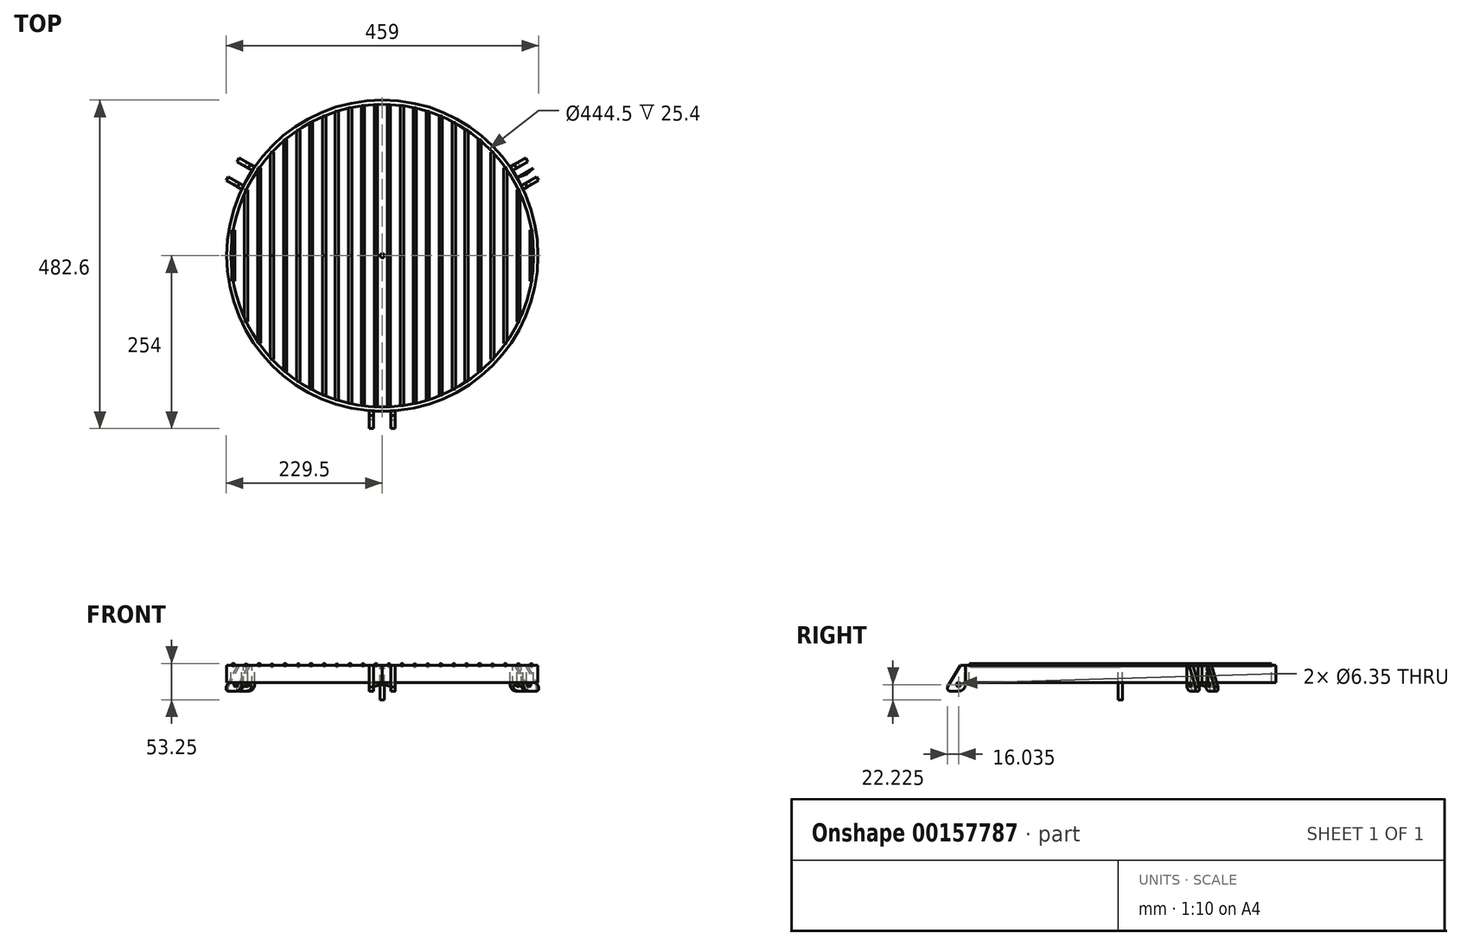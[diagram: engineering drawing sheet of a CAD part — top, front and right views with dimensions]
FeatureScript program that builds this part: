
annotation { "Feature Type Name" : "Feature", "Feature Type Description" : "" }
export const myFeature = defineFeature(function(context is Context, id is Id, definition is map)
    precondition{}
    {
        {
            var Q0;
            Q0=qCreatedBy(makeId("Top.planeOp"),FACE);
            var sketch = newSketch(context, id + "F0", { "sketchPlane" : qUnion([Q0])});
            skCircle(sketch, "E0", {"center": v(0, 0) * mm, "radius": 228.6 * mm});
            skLineSegment(sketch, "E1", {"start": v(-131.22, 187.18) * mm, "end": v(0, 0) * mm});
            skLineSegment(sketch, "E2", {"start": v(0, 0) * mm, "end": v(-96.5, -207.24) * mm});
            skLineSegment(sketch, "E3", {"start": v(0, 0) * mm, "end": v(227.72, 20.05) * mm});
            skPoint(sketch, "E4", {"position": v(-93.81, -201.48) * mm});
            skPoint(sketch, "E5", {"position": v(-127.58, 181.98) * mm});
            skPoint(sketch, "E6", {"position": v(221.4, 19.5) * mm});
            skCircle(sketch, "E7", {"center": v(0, 0) * mm, "radius": 222.25 * mm});
            skPoint(sketch, "E8", {"position": v(227.72, 20.05) * mm});
            skPoint(sketch, "E9", {"position": v(-96.5, -207.24) * mm});
            skPoint(sketch, "E10", {"position": v(-131.22, 187.18) * mm});
            skCircle(sketch, "E11", {"center": v(0, 0) * mm, "radius": 3.18 * mm});
            skSolve(sketch);
        }
        {
            var Q0;
            {var subQ0=sQuery(id+"F0.wireOp",EDGE,"E1");var subQ1=sQuery(id+"F0.wireOp",EDGE,"E0");var subQ2=makeQuery(id+"F0.imprint","INTERSECT",VERTEX,{"derivedFrom":[subQ1,subQ0]});Q0=makeQuery(id+"F0.imprint","IMPRINT",FACE,{"disambiguationData":[TD([[makeQuery(id+"F0.imprint","IMPRINT",EDGE,{"disambiguationData":[TD([[subQ2,-1.0]])],"derivedFrom":subQ1}),1.0]])]});}
            var Q1;
            {var subQ0=sQuery(id+"F0.wireOp",EDGE,"E2");var subQ1=sQuery(id+"F0.wireOp",EDGE,"E0");var subQ2=makeQuery(id+"F0.imprint","INTERSECT",VERTEX,{"derivedFrom":[subQ1,subQ0]});Q1=makeQuery(id+"F0.imprint","IMPRINT",FACE,{"disambiguationData":[TD([[makeQuery(id+"F0.imprint","IMPRINT",EDGE,{"disambiguationData":[TD([[subQ2,-1.0]])],"derivedFrom":subQ1}),1.0]])]});}
            var Q2;
            {var subQ0=sQuery(id+"F0.wireOp",EDGE,"E1");var subQ1=sQuery(id+"F0.wireOp",EDGE,"E0");var subQ2=makeQuery(id+"F0.imprint","INTERSECT",VERTEX,{"derivedFrom":[subQ1,subQ0]});Q2=makeQuery(id+"F0.imprint","IMPRINT",FACE,{"disambiguationData":[TD([[makeQuery(id+"F0.imprint","IMPRINT",EDGE,{"disambiguationData":[TD([[subQ2,1.0]])],"derivedFrom":subQ1}),1.0]])]});}
            extrude(context, id + "F1", {"entities" : qUnion([Q0, Q1, Q2]), "oppositeDirection" : true, "depth" : 25.4 * mm});
        }
        {
            var Q0;
            Q0=qCreatedBy(makeId("Top.planeOp"),FACE);
            var sketch = newSketch(context, id + "F2", { "sketchPlane" : qUnion([Q0])});
            skLineSegment(sketch, "E12", {"start": v(-221.98, 0) * mm, "end": v(222.25, 0) * mm});
            skPoint(sketch, "E13", {"position": v(-9.53, 0) * mm});
            skPoint(sketch, "E14", {"position": v(9.53, 0) * mm});
            skPoint(sketch, "E15", {"position": v(28.57, 0) * mm});
            skPoint(sketch, "E16", {"position": v(66.67, 0) * mm});
            skPoint(sketch, "E17", {"position": v(47.62, 0) * mm});
            skPoint(sketch, "E18", {"position": v(85.72, 0) * mm});
            skPoint(sketch, "E19", {"position": v(104.77, 0) * mm});
            skPoint(sketch, "E20", {"position": v(123.82, 0) * mm});
            skPoint(sketch, "E21", {"position": v(142.88, 0) * mm});
            skPoint(sketch, "E22", {"position": v(161.93, 0) * mm});
            skPoint(sketch, "E23", {"position": v(180.98, 0) * mm});
            skPoint(sketch, "E24", {"position": v(200.03, 0) * mm});
            skPoint(sketch, "E25", {"position": v(219.08, 0) * mm});
            skPoint(sketch, "E26", {"position": v(-28.57, 0) * mm});
            skPoint(sketch, "E27", {"position": v(-47.62, 0) * mm});
            skPoint(sketch, "E28", {"position": v(-66.67, 0) * mm});
            skPoint(sketch, "E29", {"position": v(-85.72, 0) * mm});
            skPoint(sketch, "E30", {"position": v(-104.77, 0) * mm});
            skPoint(sketch, "E31", {"position": v(-123.82, 0) * mm});
            skPoint(sketch, "E32", {"position": v(-142.88, 0) * mm});
            skPoint(sketch, "E33", {"position": v(-161.93, 0) * mm});
            skPoint(sketch, "E34", {"position": v(-180.98, 0) * mm});
            skPoint(sketch, "E35", {"position": v(-200.03, 0) * mm});
            skPoint(sketch, "E36", {"position": v(-219.08, 0) * mm});
            skSolve(sketch);
        }
        {
            var Q0;
            Q0=qCreatedBy(makeId("Front.planeOp"),FACE);
            var sketch = newSketch(context, id + "F3", { "sketchPlane" : qUnion([Q0])});
            skCircle(sketch, "E37", {"center": v(-219.08, 0) * mm, "radius": 2.38 * mm});
            skCircle(sketch, "E38", {"center": v(-200.35, -0.55) * mm, "radius": 2.38 * mm});
            skCircle(sketch, "E39", {"center": v(-180.87, 0.07) * mm, "radius": 2.38 * mm});
            skCircle(sketch, "E40", {"center": v(-162.2, -0.64) * mm, "radius": 2.38 * mm});
            skCircle(sketch, "E41", {"center": v(-143.01, 0.04) * mm, "radius": 2.38 * mm});
            skCircle(sketch, "E42", {"center": v(-123.47, -0.4) * mm, "radius": 2.38 * mm});
            skCircle(sketch, "E43", {"center": v(-104.72, 0) * mm, "radius": 2.38 * mm});
            skCircle(sketch, "E44", {"center": v(-85.3, -0.08) * mm, "radius": 2.38 * mm});
            skCircle(sketch, "E45", {"center": v(-66.89, -0.46) * mm, "radius": 2.38 * mm});
            skCircle(sketch, "E46", {"center": v(-47.42, 0.02) * mm, "radius": 2.38 * mm});
            skCircle(sketch, "E47", {"center": v(-28.43, -0.18) * mm, "radius": 2.38 * mm});
            skCircle(sketch, "E48", {"center": v(-9.43, -0.1) * mm, "radius": 2.38 * mm});
            skCircle(sketch, "E49", {"center": v(9.57, -0.32) * mm, "radius": 2.38 * mm});
            skCircle(sketch, "E50", {"center": v(29.03, 0.02) * mm, "radius": 2.38 * mm});
            skCircle(sketch, "E51", {"center": v(47.58, -0.6) * mm, "radius": 2.38 * mm});
            skCircle(sketch, "E52", {"center": v(66.61, -0.4) * mm, "radius": 2.38 * mm});
            skCircle(sketch, "E53", {"center": v(85.79, -0.15) * mm, "radius": 2.38 * mm});
            skCircle(sketch, "E54", {"center": v(104.94, -0.18) * mm, "radius": 2.38 * mm});
            skCircle(sketch, "E55", {"center": v(123.67, -0.21) * mm, "radius": 2.38 * mm});
            skCircle(sketch, "E56", {"center": v(142.84, 0.04) * mm, "radius": 2.38 * mm});
            skCircle(sketch, "E57", {"center": v(161.77, -0.53) * mm, "radius": 2.38 * mm});
            skCircle(sketch, "E58", {"center": v(180.82, -0.13) * mm, "radius": 2.38 * mm});
            skCircle(sketch, "E59", {"center": v(199.95, -0.34) * mm, "radius": 2.38 * mm});
            skCircle(sketch, "E60", {"center": v(218.97, -0.34) * mm, "radius": 2.38 * mm});
            skSolve(sketch);
        }
        {
            var Q0;
            Q0=makeQuery(id+"F3.imprint","IMPRINT",FACE,{"disambiguationData":[TD([[makeQuery(id+"F3.imprint","IMPRINT",EDGE,{"derivedFrom":sQuery(id+"F3.wireOp",EDGE,"E49")}),1.0]])]});
            extrude(context, id + "F4", {"entities" : qUnion([Q0]), "oppositeDirection" : true, "depth" : 222.05 * mm});
        }
        {
            var Q0;
            Q0=makeQuery(id+"F3.imprint","IMPRINT",FACE,{"disambiguationData":[TD([[makeQuery(id+"F3.imprint","IMPRINT",EDGE,{"derivedFrom":sQuery(id+"F3.wireOp",EDGE,"E49")}),1.0]])]});
            extrude(context, id + "F5", {"entities" : qUnion([Q0]), "operationType" : NewBodyOperationType.ADD, "depth" : 222.05 * mm});
        }
        {
            var Q0;
            Q0=makeQuery(id+"F3.imprint","IMPRINT",FACE,{"disambiguationData":[TD([[makeQuery(id+"F3.imprint","IMPRINT",EDGE,{"derivedFrom":sQuery(id+"F3.wireOp",EDGE,"E48")}),1.0]])]});
            extrude(context, id + "F6", {"entities" : qUnion([Q0]), "depth" : 222.05 * mm});
        }
        {
            var Q0;
            Q0=makeQuery(id+"F3.imprint","IMPRINT",FACE,{"disambiguationData":[TD([[makeQuery(id+"F3.imprint","IMPRINT",EDGE,{"derivedFrom":sQuery(id+"F3.wireOp",EDGE,"E48")}),1.0]])]});
            extrude(context, id + "F7", {"entities" : qUnion([Q0]), "oppositeDirection" : true, "depth" : 222.05 * mm});
        }
        {
            var Q0;
            Q0=makeQuery(id+"F3.imprint","IMPRINT",FACE,{"disambiguationData":[TD([[makeQuery(id+"F3.imprint","IMPRINT",EDGE,{"derivedFrom":sQuery(id+"F3.wireOp",EDGE,"E47")}),1.0]])]});
            extrude(context, id + "F8", {"entities" : qUnion([Q0]), "depth" : 220.4 * mm});
        }
        {
            var Q0;
            Q0=makeQuery(id+"F3.imprint","IMPRINT",FACE,{"disambiguationData":[TD([[makeQuery(id+"F3.imprint","IMPRINT",EDGE,{"derivedFrom":sQuery(id+"F3.wireOp",EDGE,"E50")}),1.0]])]});
            extrude(context, id + "F9", {"entities" : qUnion([Q0]), "depth" : 220.4 * mm});
        }
        {
            var Q0;
            Q0=makeQuery(id+"F3.imprint","IMPRINT",FACE,{"disambiguationData":[TD([[makeQuery(id+"F3.imprint","IMPRINT",EDGE,{"derivedFrom":sQuery(id+"F3.wireOp",EDGE,"E50")}),1.0]])]});
            extrude(context, id + "F10", {"entities" : qUnion([Q0]), "oppositeDirection" : true, "depth" : 220.4 * mm});
        }
        {
            var Q0;
            Q0=makeQuery(id+"F3.imprint","IMPRINT",FACE,{"disambiguationData":[TD([[makeQuery(id+"F3.imprint","IMPRINT",EDGE,{"derivedFrom":sQuery(id+"F3.wireOp",EDGE,"E47")}),1.0]])]});
            extrude(context, id + "F11", {"entities" : qUnion([Q0]), "oppositeDirection" : true, "depth" : 220.4 * mm});
        }
        {
            var Q0;
            Q0=makeQuery(id+"F3.imprint","IMPRINT",FACE,{"disambiguationData":[TD([[makeQuery(id+"F3.imprint","IMPRINT",EDGE,{"derivedFrom":sQuery(id+"F3.wireOp",EDGE,"E51")}),1.0]])]});
            extrude(context, id + "F12", {"entities" : qUnion([Q0]), "depth" : 217.1 * mm});
        }
        {
            var Q0;
            Q0=makeQuery(id+"F3.imprint","IMPRINT",FACE,{"disambiguationData":[TD([[makeQuery(id+"F3.imprint","IMPRINT",EDGE,{"derivedFrom":sQuery(id+"F3.wireOp",EDGE,"E51")}),1.0]])]});
            extrude(context, id + "F13", {"entities" : qUnion([Q0]), "oppositeDirection" : true, "depth" : 217.1 * mm});
        }
        {
            var Q0;
            Q0=makeQuery(id+"F3.imprint","IMPRINT",FACE,{"disambiguationData":[TD([[makeQuery(id+"F3.imprint","IMPRINT",EDGE,{"derivedFrom":sQuery(id+"F3.wireOp",EDGE,"E46")}),1.0]])]});
            extrude(context, id + "F14", {"entities" : qUnion([Q0]), "depth" : 217.1 * mm});
        }
        {
            var Q0;
            Q0=makeQuery(id+"F3.imprint","IMPRINT",FACE,{"disambiguationData":[TD([[makeQuery(id+"F3.imprint","IMPRINT",EDGE,{"derivedFrom":sQuery(id+"F3.wireOp",EDGE,"E46")}),1.0]])]});
            extrude(context, id + "F15", {"entities" : qUnion([Q0]), "oppositeDirection" : true, "depth" : 217.1 * mm});
        }
        {
            var Q0;
            Q0=makeQuery(id+"F3.imprint","IMPRINT",FACE,{"disambiguationData":[TD([[makeQuery(id+"F3.imprint","IMPRINT",EDGE,{"derivedFrom":sQuery(id+"F3.wireOp",EDGE,"E52")}),1.0]])]});
            extrude(context, id + "F16", {"entities" : qUnion([Q0]), "depth" : 212 * mm});
        }
        {
            var Q0;
            Q0=makeQuery(id+"F3.imprint","IMPRINT",FACE,{"disambiguationData":[TD([[makeQuery(id+"F3.imprint","IMPRINT",EDGE,{"derivedFrom":sQuery(id+"F3.wireOp",EDGE,"E45")}),1.0]])]});
            extrude(context, id + "F17", {"entities" : qUnion([Q0]), "depth" : 212 * mm});
        }
        {
            var Q0;
            Q0=makeQuery(id+"F3.imprint","IMPRINT",FACE,{"disambiguationData":[TD([[makeQuery(id+"F3.imprint","IMPRINT",EDGE,{"derivedFrom":sQuery(id+"F3.wireOp",EDGE,"E52")}),1.0]])]});
            extrude(context, id + "F18", {"entities" : qUnion([Q0]), "oppositeDirection" : true, "depth" : 212 * mm});
        }
        {
            var Q0;
            Q0=makeQuery(id+"F3.imprint","IMPRINT",FACE,{"disambiguationData":[TD([[makeQuery(id+"F3.imprint","IMPRINT",EDGE,{"derivedFrom":sQuery(id+"F3.wireOp",EDGE,"E45")}),1.0]])]});
            extrude(context, id + "F19", {"entities" : qUnion([Q0]), "oppositeDirection" : true, "depth" : 212 * mm});
        }
        {
            var Q0;
            Q0=makeQuery(id+"F3.imprint","IMPRINT",FACE,{"disambiguationData":[TD([[makeQuery(id+"F3.imprint","IMPRINT",EDGE,{"derivedFrom":sQuery(id+"F3.wireOp",EDGE,"E53")}),1.0]])]});
            extrude(context, id + "F20", {"entities" : qUnion([Q0]), "depth" : 205.05 * mm});
        }
        {
            var Q0;
            Q0=makeQuery(id+"F3.imprint","IMPRINT",FACE,{"disambiguationData":[TD([[makeQuery(id+"F3.imprint","IMPRINT",EDGE,{"derivedFrom":sQuery(id+"F3.wireOp",EDGE,"E44")}),1.0]])]});
            extrude(context, id + "F21", {"entities" : qUnion([Q0]), "depth" : 205.05 * mm});
        }
        {
            var Q0;
            Q0=makeQuery(id+"F3.imprint","IMPRINT",FACE,{"disambiguationData":[TD([[makeQuery(id+"F3.imprint","IMPRINT",EDGE,{"derivedFrom":sQuery(id+"F3.wireOp",EDGE,"E53")}),1.0]])]});
            extrude(context, id + "F22", {"entities" : qUnion([Q0]), "oppositeDirection" : true, "depth" : 205.05 * mm});
        }
        {
            var Q0;
            Q0=makeQuery(id+"F3.imprint","IMPRINT",FACE,{"disambiguationData":[TD([[makeQuery(id+"F3.imprint","IMPRINT",EDGE,{"derivedFrom":sQuery(id+"F3.wireOp",EDGE,"E44")}),1.0]])]});
            extrude(context, id + "F23", {"entities" : qUnion([Q0]), "oppositeDirection" : true, "depth" : 205.05 * mm});
        }
        {
            var Q0;
            Q0=makeQuery(id+"F3.imprint","IMPRINT",FACE,{"disambiguationData":[TD([[makeQuery(id+"F3.imprint","IMPRINT",EDGE,{"derivedFrom":sQuery(id+"F3.wireOp",EDGE,"E54")}),1.0]])]});
            extrude(context, id + "F24", {"entities" : qUnion([Q0]), "depth" : 196 * mm});
        }
        {
            var Q0;
            Q0=makeQuery(id+"F3.imprint","IMPRINT",FACE,{"disambiguationData":[TD([[makeQuery(id+"F3.imprint","IMPRINT",EDGE,{"derivedFrom":sQuery(id+"F3.wireOp",EDGE,"E54")}),1.0]])]});
            extrude(context, id + "F25", {"entities" : qUnion([Q0]), "oppositeDirection" : true, "depth" : 196 * mm});
        }
        {
            var Q0;
            Q0=makeQuery(id+"F3.imprint","IMPRINT",FACE,{"disambiguationData":[TD([[makeQuery(id+"F3.imprint","IMPRINT",EDGE,{"derivedFrom":sQuery(id+"F3.wireOp",EDGE,"E43")}),1.0]])]});
            extrude(context, id + "F26", {"entities" : qUnion([Q0]), "depth" : 196 * mm});
        }
        {
            var Q0;
            Q0=makeQuery(id+"F3.imprint","IMPRINT",FACE,{"disambiguationData":[TD([[makeQuery(id+"F3.imprint","IMPRINT",EDGE,{"derivedFrom":sQuery(id+"F3.wireOp",EDGE,"E43")}),1.0]])]});
            extrude(context, id + "F27", {"entities" : qUnion([Q0]), "oppositeDirection" : true, "depth" : 196 * mm});
        }
        {
            var Q0;
            Q0=makeQuery(id+"F3.imprint","IMPRINT",FACE,{"disambiguationData":[TD([[makeQuery(id+"F3.imprint","IMPRINT",EDGE,{"derivedFrom":sQuery(id+"F3.wireOp",EDGE,"E42")}),1.0]])]});
            extrude(context, id + "F28", {"entities" : qUnion([Q0]), "depth" : 184.56 * mm});
        }
        {
            var Q0;
            Q0=makeQuery(id+"F3.imprint","IMPRINT",FACE,{"disambiguationData":[TD([[makeQuery(id+"F3.imprint","IMPRINT",EDGE,{"derivedFrom":sQuery(id+"F3.wireOp",EDGE,"E42")}),1.0]])]});
            extrude(context, id + "F29", {"entities" : qUnion([Q0]), "oppositeDirection" : true, "depth" : 184.56 * mm});
        }
        {
            var Q0;
            Q0=makeQuery(id+"F3.imprint","IMPRINT",FACE,{"disambiguationData":[TD([[makeQuery(id+"F3.imprint","IMPRINT",EDGE,{"derivedFrom":sQuery(id+"F3.wireOp",EDGE,"E55")}),1.0]])]});
            extrude(context, id + "F30", {"entities" : qUnion([Q0]), "oppositeDirection" : true, "depth" : 184.56 * mm});
        }
        {
            var Q0;
            Q0=makeQuery(id+"F3.imprint","IMPRINT",FACE,{"disambiguationData":[TD([[makeQuery(id+"F3.imprint","IMPRINT",EDGE,{"derivedFrom":sQuery(id+"F3.wireOp",EDGE,"E55")}),1.0]])]});
            extrude(context, id + "F31", {"entities" : qUnion([Q0]), "depth" : 184.56 * mm});
        }
        {
            var Q0;
            Q0=makeQuery(id+"F3.imprint","IMPRINT",FACE,{"disambiguationData":[TD([[makeQuery(id+"F3.imprint","IMPRINT",EDGE,{"derivedFrom":sQuery(id+"F3.wireOp",EDGE,"E41")}),1.0]])]});
            extrude(context, id + "F32", {"entities" : qUnion([Q0]), "oppositeDirection" : true, "depth" : 170.24 * mm});
        }
        {
            var Q0;
            Q0=makeQuery(id+"F3.imprint","IMPRINT",FACE,{"disambiguationData":[TD([[makeQuery(id+"F3.imprint","IMPRINT",EDGE,{"derivedFrom":sQuery(id+"F3.wireOp",EDGE,"E41")}),1.0]])]});
            extrude(context, id + "F33", {"entities" : qUnion([Q0]), "depth" : 170.24 * mm});
        }
        {
            var Q0;
            Q0=makeQuery(id+"F3.imprint","IMPRINT",FACE,{"disambiguationData":[TD([[makeQuery(id+"F3.imprint","IMPRINT",EDGE,{"derivedFrom":sQuery(id+"F3.wireOp",EDGE,"E56")}),1.0]])]});
            extrude(context, id + "F34", {"entities" : qUnion([Q0]), "oppositeDirection" : true, "depth" : 170.24 * mm});
        }
        {
            var Q0;
            Q0=makeQuery(id+"F3.imprint","IMPRINT",FACE,{"disambiguationData":[TD([[makeQuery(id+"F3.imprint","IMPRINT",EDGE,{"derivedFrom":sQuery(id+"F3.wireOp",EDGE,"E56")}),1.0]])]});
            extrude(context, id + "F35", {"entities" : qUnion([Q0]), "depth" : 170.24 * mm});
        }
        {
            var Q0;
            Q0=makeQuery(id+"F3.imprint","IMPRINT",FACE,{"disambiguationData":[TD([[makeQuery(id+"F3.imprint","IMPRINT",EDGE,{"derivedFrom":sQuery(id+"F3.wireOp",EDGE,"E40")}),1.0]])]});
            extrude(context, id + "F36", {"entities" : qUnion([Q0]), "depth" : 152.23 * mm});
        }
        {
            var Q0;
            Q0=makeQuery(id+"F3.imprint","IMPRINT",FACE,{"disambiguationData":[TD([[makeQuery(id+"F3.imprint","IMPRINT",EDGE,{"derivedFrom":sQuery(id+"F3.wireOp",EDGE,"E57")}),1.0]])]});
            extrude(context, id + "F37", {"entities" : qUnion([Q0]), "oppositeDirection" : true, "depth" : 152.23 * mm});
        }
        {
            var Q0;
            Q0=makeQuery(id+"F3.imprint","IMPRINT",FACE,{"disambiguationData":[TD([[makeQuery(id+"F3.imprint","IMPRINT",EDGE,{"derivedFrom":sQuery(id+"F3.wireOp",EDGE,"E57")}),1.0]])]});
            extrude(context, id + "F38", {"entities" : qUnion([Q0]), "depth" : 152.23 * mm});
        }
        {
            var Q0;
            Q0=makeQuery(id+"F3.imprint","IMPRINT",FACE,{"disambiguationData":[TD([[makeQuery(id+"F3.imprint","IMPRINT",EDGE,{"derivedFrom":sQuery(id+"F3.wireOp",EDGE,"E40")}),1.0]])]});
            extrude(context, id + "F39", {"entities" : qUnion([Q0]), "oppositeDirection" : true, "depth" : 152.23 * mm});
        }
        {
            var Q0;
            Q0=makeQuery(id+"F3.imprint","IMPRINT",FACE,{"disambiguationData":[TD([[makeQuery(id+"F3.imprint","IMPRINT",EDGE,{"derivedFrom":sQuery(id+"F3.wireOp",EDGE,"E39")}),1.0]])]});
            extrude(context, id + "F40", {"entities" : qUnion([Q0]), "depth" : 129 * mm});
        }
        {
            var Q0;
            Q0=makeQuery(id+"F3.imprint","IMPRINT",FACE,{"disambiguationData":[TD([[makeQuery(id+"F3.imprint","IMPRINT",EDGE,{"derivedFrom":sQuery(id+"F3.wireOp",EDGE,"E39")}),1.0]])]});
            extrude(context, id + "F41", {"entities" : qUnion([Q0]), "oppositeDirection" : true, "depth" : 129 * mm});
        }
        {
            var Q0;
            Q0=makeQuery(id+"F3.imprint","IMPRINT",FACE,{"disambiguationData":[TD([[makeQuery(id+"F3.imprint","IMPRINT",EDGE,{"derivedFrom":sQuery(id+"F3.wireOp",EDGE,"E58")}),1.0]])]});
            extrude(context, id + "F42", {"entities" : qUnion([Q0]), "depth" : 129 * mm});
        }
        {
            var Q0;
            Q0=makeQuery(id+"F3.imprint","IMPRINT",FACE,{"disambiguationData":[TD([[makeQuery(id+"F3.imprint","IMPRINT",EDGE,{"derivedFrom":sQuery(id+"F3.wireOp",EDGE,"E58")}),1.0]])]});
            extrude(context, id + "F43", {"entities" : qUnion([Q0]), "oppositeDirection" : true, "depth" : 129 * mm});
        }
        {
            var Q0;
            Q0=makeQuery(id+"F3.imprint","IMPRINT",FACE,{"disambiguationData":[TD([[makeQuery(id+"F3.imprint","IMPRINT",EDGE,{"derivedFrom":sQuery(id+"F3.wireOp",EDGE,"E38")}),1.0]])]});
            extrude(context, id + "F44", {"entities" : qUnion([Q0]), "depth" : 96.88 * mm});
        }
        {
            var Q0;
            Q0=makeQuery(id+"F3.imprint","IMPRINT",FACE,{"disambiguationData":[TD([[makeQuery(id+"F3.imprint","IMPRINT",EDGE,{"derivedFrom":sQuery(id+"F3.wireOp",EDGE,"E38")}),1.0]])]});
            extrude(context, id + "F45", {"entities" : qUnion([Q0]), "oppositeDirection" : true, "depth" : 96.88 * mm});
        }
        {
            var Q0;
            Q0=makeQuery(id+"F3.imprint","IMPRINT",FACE,{"disambiguationData":[TD([[makeQuery(id+"F3.imprint","IMPRINT",EDGE,{"derivedFrom":sQuery(id+"F3.wireOp",EDGE,"E59")}),1.0]])]});
            extrude(context, id + "F46", {"entities" : qUnion([Q0]), "depth" : 96.88 * mm});
        }
        {
            var Q0;
            Q0=makeQuery(id+"F3.imprint","IMPRINT",FACE,{"disambiguationData":[TD([[makeQuery(id+"F3.imprint","IMPRINT",EDGE,{"derivedFrom":sQuery(id+"F3.wireOp",EDGE,"E59")}),1.0]])]});
            extrude(context, id + "F47", {"entities" : qUnion([Q0]), "oppositeDirection" : true, "depth" : 96.88 * mm});
        }
        {
            var Q0;
            Q0=makeQuery(id+"F3.imprint","IMPRINT",FACE,{"disambiguationData":[TD([[makeQuery(id+"F3.imprint","IMPRINT",EDGE,{"derivedFrom":sQuery(id+"F3.wireOp",EDGE,"E37")}),1.0]])]});
            extrude(context, id + "F48", {"entities" : qUnion([Q0]), "depth" : 37.43 * mm});
        }
        {
            var Q0;
            Q0=makeQuery(id+"F3.imprint","IMPRINT",FACE,{"disambiguationData":[TD([[makeQuery(id+"F3.imprint","IMPRINT",EDGE,{"derivedFrom":sQuery(id+"F3.wireOp",EDGE,"E37")}),1.0]])]});
            extrude(context, id + "F49", {"entities" : qUnion([Q0]), "oppositeDirection" : true, "depth" : 37.43 * mm});
        }
        {
            var Q0;
            Q0=makeQuery(id+"F3.imprint","IMPRINT",FACE,{"disambiguationData":[TD([[makeQuery(id+"F3.imprint","IMPRINT",EDGE,{"derivedFrom":sQuery(id+"F3.wireOp",EDGE,"E60")}),1.0]])]});
            extrude(context, id + "F50", {"entities" : qUnion([Q0]), "depth" : 37.43 * mm});
        }
        {
            var Q0;
            Q0=makeQuery(id+"F3.imprint","IMPRINT",FACE,{"disambiguationData":[TD([[makeQuery(id+"F3.imprint","IMPRINT",EDGE,{"derivedFrom":sQuery(id+"F3.wireOp",EDGE,"E60")}),1.0]])]});
            extrude(context, id + "F51", {"entities" : qUnion([Q0]), "oppositeDirection" : true, "depth" : 37.43 * mm});
        }
        {
            var Q0;
            Q0=makeQuery(id+"F1.opExtrude","CAP_FACE",FACE,{"disambiguationData":[OSD([sQuery(id+"F0.wireOp",EDGE,"E0"),sQuery(id+"F0.wireOp",EDGE,"E7")])],"isStart":true});
            var sketch = newSketch(context, id + "F52", { "sketchPlane" : qUnion([Q0])});
            skLineSegment(sketch, "E61", {"start": v(0, 0) * mm, "end": v(0, -264.56) * mm});
            skLineSegment(sketch, "E62", {"start": v(0, 0) * mm, "end": v(222.27, 128.33) * mm});
            skLineSegment(sketch, "E63", {"start": v(0, 0) * mm, "end": v(-233.5, 134.81) * mm});
            skLineSegment(sketch, "E64", {"start": v(197.97, 114.3) * mm, "end": v(191.62, 125.3) * mm});
            skLineSegment(sketch, "E65", {"start": v(197.97, 114.3) * mm, "end": v(204.32, 103.3) * mm});
            skLineSegment(sketch, "E66", {"start": v(191.62, 125.3) * mm, "end": v(213.62, 138) * mm});
            skLineSegment(sketch, "E67", {"start": v(213.62, 138) * mm, "end": v(210.45, 143.5) * mm});
            skLineSegment(sketch, "E68", {"start": v(210.45, 143.5) * mm, "end": v(187.76, 130.4) * mm});
            skLineSegment(sketch, "E69", {"start": v(197.97, 114.3) * mm, "end": v(212.05, 119.52) * mm});
            skLineSegment(sketch, "E70", {"start": v(212.05, 119.52) * mm, "end": v(222.27, 128.33) * mm});
            skSolve(sketch);
        }
        {
            var Q0;
            {var subQ1=sQuery(id+"F52.wireOp",EDGE,"E64");Q0=makeQuery(id+"F52.imprint","IMPRINT",FACE,{"disambiguationData":[TD([[makeQuery(id+"F52.imprint","IMPRINT",EDGE,{"derivedFrom":subQ1}),1.0]])]});}
            extrude(context, id + "F53", {"entities" : qUnion([Q0]), "oppositeDirection" : true, "depth" : 38.1 * mm});
        }
        {
            var Q0;
            {var subQ2=sQuery(id+"F52.wireOp",EDGE,"E69");Q0=makeQuery(id+"F52.imprint","IMPRINT",FACE,{"disambiguationData":[TD([[makeQuery(id+"F52.imprint","IMPRINT",EDGE,{"derivedFrom":subQ2}),1.0]])]});}
            extrude(context, id + "F54", {"entities" : qUnion([Q0]), "oppositeDirection" : true, "depth" : 25.4 * mm});
        }
        {
            var Q0;
            Q0=makeQuery(id+"F53.opExtrude","SWEPT_FACE",FACE,{"disambiguationData":[OSD([sQuery(id+"F52.wireOp",EDGE,"E68")])]});
            var sketch = newSketch(context, id + "F55", { "sketchPlane" : qUnion([Q0])});
            skLineSegment(sketch, "E71", {"start": v(-254, 0) * mm, "end": v(-234.95, 0) * mm});
            skLineSegment(sketch, "E72", {"start": v(-234.95, 0) * mm, "end": v(-254, -31.75) * mm});
            skLineSegment(sketch, "E73", {"start": v(-254, -31.75) * mm, "end": v(-254, 0) * mm});
            skLineSegment(sketch, "E74.bottom", {"start": v(-227.8, -38.1) * mm, "end": v(-237.96, -38.1) * mm});
            skLineSegment(sketch, "E74.top", {"start": v(-227.8, -28.58) * mm, "end": v(-237.96, -28.58) * mm});
            skLineSegment(sketch, "E74.left", {"start": v(-227.8, -38.1) * mm, "end": v(-227.8, -28.58) * mm});
            skLineSegment(sketch, "E74.right", {"start": v(-237.96, -38.1) * mm, "end": v(-237.96, -28.58) * mm});
            skCircle(sketch, "E75", {"center": v(-237.96, -28.58) * mm, "radius": 3.18 * mm});
            skSolve(sketch);
        }
        {
            var Q0;
            Q0=makeQuery(id+"F53.opExtrude","CAP_EDGE",EDGE,{"disambiguationData":[OSD([sQuery(id+"F0.wireOp",EDGE,"E0")])],"isStart":false});
            fillet(context, id + "F56", {"entities" : qUnion([Q0]), "radius" : 9.52 * mm, "tangentPropagation" : true, "allowEdgeOverflow" : false});
        }
        {
            var Q0;
            Q0=makeQuery(id+"F55.imprint","IMPRINT",FACE,{"disambiguationData":[TD([[makeQuery(id+"F55.imprint","IMPRINT",EDGE,{"derivedFrom":sQuery(id+"F55.wireOp",EDGE,"E71")}),-1.0]])]});
            var Q1;
            {var subQ0=sQuery(id+"F55.wireOp",EDGE,"E74.right");var subQ1=sQuery(id+"F55.wireOp",EDGE,"E74.top");var subQ2=makeQuery(id+"F55.imprint","INTERSECT",VERTEX,{"derivedFrom":[subQ1,subQ0]});Q1=makeQuery(id+"F55.imprint","IMPRINT",FACE,{"disambiguationData":[TD([[makeQuery(id+"F55.imprint","IMPRINT",EDGE,{"disambiguationData":[TD([[subQ2,1.0]])],"derivedFrom":subQ1}),1.0]])]});}
            var Q2;
            {var subQ0=sQuery(id+"F55.wireOp",EDGE,"E74.right");var subQ1=sQuery(id+"F55.wireOp",EDGE,"E74.top");var subQ2=makeQuery(id+"F55.imprint","INTERSECT",VERTEX,{"derivedFrom":[subQ1,subQ0]});Q2=makeQuery(id+"F55.imprint","IMPRINT",FACE,{"disambiguationData":[TD([[makeQuery(id+"F55.imprint","IMPRINT",EDGE,{"disambiguationData":[TD([[subQ2,1.0]])],"derivedFrom":subQ1}),-1.0]])]});}
            extrude(context, id + "F57", {"entities" : qUnion([Q0, Q1, Q2]), "operationType" : NewBodyOperationType.REMOVE, "oppositeDirection" : true, "depth" : 6.35 * mm});
        }
        {
            var Q0;
            Q0=makeQuery(id+"F57.boolean.opBoolean","COPY",EDGE,{"derivedFrom":makeQuery(id+"F57.opExtrude","SWEPT_EDGE",EDGE,{"disambiguationData":[OSD([sQuery(id+"F52.wireOp",EDGE,"E68"),sQuery(id+"F55.wireOp",EDGE,"E71"),sQuery(id+"F55.wireOp",EDGE,"E72")])]})});
            var Q1;
            Q1=makeQuery(id+"F57.boolean.opBoolean","COPY",EDGE,{"derivedFrom":makeQuery(id+"F57.opExtrude","SWEPT_EDGE",EDGE,{"disambiguationData":[OSD([sQuery(id+"F52.wireOp",EDGE,"E67"),sQuery(id+"F52.wireOp",EDGE,"E68"),sQuery(id+"F55.wireOp",EDGE,"E72"),sQuery(id+"F55.wireOp",EDGE,"E73")])]})});
            var Q2;
            Q2=makeQuery(id+"F53.opExtrude","CAP_EDGE",EDGE,{"disambiguationData":[OSD([sQuery(id+"F52.wireOp",EDGE,"E67")])],"isStart":false});
            fillet(context, id + "F58", {"entities" : qUnion([Q0, Q1, Q2]), "radius" : 3.17 * mm, "tangentPropagation" : true, "allowEdgeOverflow" : false});
        }
        {
            var Q0;
            Q0=makeQuery(id+"F53.opExtrude","SWEPT_BODY",BODY,{"disambiguationData":[OSD([sQuery(id+"F0.wireOp",EDGE,"E0"),sQuery(id+"F52.wireOp",EDGE,"E64"),sQuery(id+"F52.wireOp",EDGE,"E66"),sQuery(id+"F52.wireOp",EDGE,"E67"),sQuery(id+"F52.wireOp",EDGE,"E68")])]});
            var Q1;
            Q1=makeQuery(id+"F54.opExtrude","SWEPT_FACE",FACE,{"disambiguationData":[OSD([sQuery(id+"F52.wireOp",EDGE,"E62")])]});
            mirror(context, id + "F59", {"entities" : qUnion([Q0]), "mirrorPlane" : qUnion([Q1])});
        }
        {
            var Q0;
            {var subQ1=sQuery(id+"F0.wireOp",EDGE,"E2");var subQ3=sQuery(id+"F0.wireOp",EDGE,"E11");var subQ4=makeQuery(id+"F0.imprint","INTERSECT",VERTEX,{"derivedFrom":[subQ1,subQ3]});Q0=makeQuery(id+"F0.imprint","IMPRINT",FACE,{"disambiguationData":[TD([[makeQuery(id+"F0.imprint","IMPRINT",EDGE,{"disambiguationData":[TD([[subQ4,-1.0]])],"derivedFrom":subQ3}),1.0]])]});}
            var Q1;
            {var subQ1=sQuery(id+"F0.wireOp",EDGE,"E1");var subQ3=sQuery(id+"F0.wireOp",EDGE,"E11");var subQ4=makeQuery(id+"F0.imprint","INTERSECT",VERTEX,{"derivedFrom":[subQ1,subQ3]});Q1=makeQuery(id+"F0.imprint","IMPRINT",FACE,{"disambiguationData":[TD([[makeQuery(id+"F0.imprint","IMPRINT",EDGE,{"disambiguationData":[TD([[subQ4,-1.0]])],"derivedFrom":subQ3}),1.0]])]});}
            var Q2;
            {var subQ1=sQuery(id+"F0.wireOp",EDGE,"E1");var subQ3=sQuery(id+"F0.wireOp",EDGE,"E11");var subQ4=makeQuery(id+"F0.imprint","INTERSECT",VERTEX,{"derivedFrom":[subQ1,subQ3]});Q2=makeQuery(id+"F0.imprint","IMPRINT",FACE,{"disambiguationData":[TD([[makeQuery(id+"F0.imprint","IMPRINT",EDGE,{"disambiguationData":[TD([[subQ4,1.0]])],"derivedFrom":subQ3}),1.0]])]});}
            extrude(context, id + "F60", {"entities" : qUnion([Q0, Q1, Q2]), "oppositeDirection" : true, "depth" : 50.8 * mm});
        }
        {
            var Q0;
            Q0=makeQuery(id+"F53.opExtrude","SWEPT_BODY",BODY,{"disambiguationData":[OSD([sQuery(id+"F0.wireOp",EDGE,"E0"),sQuery(id+"F52.wireOp",EDGE,"E64"),sQuery(id+"F52.wireOp",EDGE,"E66"),sQuery(id+"F52.wireOp",EDGE,"E67"),sQuery(id+"F52.wireOp",EDGE,"E68")])]});
            var Q1;
            Q1=makeQuery(id+"F59.opPattern","COPY",BODY,{"derivedFrom":makeQuery(id+"F53.opExtrude","SWEPT_BODY",BODY,{"disambiguationData":[OSD([sQuery(id+"F0.wireOp",EDGE,"E0"),sQuery(id+"F52.wireOp",EDGE,"E64"),sQuery(id+"F52.wireOp",EDGE,"E66"),sQuery(id+"F52.wireOp",EDGE,"E67"),sQuery(id+"F52.wireOp",EDGE,"E68")])]}),"instanceName":"1"});
            var Q2;
            Q2=makeQuery(id+"F60.opExtrude","SWEPT_FACE",FACE,{"disambiguationData":[OSD([sQuery(id+"F0.wireOp",EDGE,"E11")])]});
            transform(context, id + "F61", {"entities" : qUnion([Q0, Q1]), "transformType" : TransformType.ROTATION, "transformAxis" : qUnion([Q2]), "angle" : 120 * degree, "makeCopy" : true});
        }
        {
            var Q0;
            Q0=makeQuery(id+"F53.opExtrude","SWEPT_BODY",BODY,{"disambiguationData":[OSD([sQuery(id+"F0.wireOp",EDGE,"E0"),sQuery(id+"F52.wireOp",EDGE,"E64"),sQuery(id+"F52.wireOp",EDGE,"E66"),sQuery(id+"F52.wireOp",EDGE,"E67"),sQuery(id+"F52.wireOp",EDGE,"E68")])]});
            var Q1;
            Q1=makeQuery(id+"F59.opPattern","COPY",BODY,{"derivedFrom":makeQuery(id+"F53.opExtrude","SWEPT_BODY",BODY,{"disambiguationData":[OSD([sQuery(id+"F0.wireOp",EDGE,"E0"),sQuery(id+"F52.wireOp",EDGE,"E64"),sQuery(id+"F52.wireOp",EDGE,"E66"),sQuery(id+"F52.wireOp",EDGE,"E67"),sQuery(id+"F52.wireOp",EDGE,"E68")])]}),"instanceName":"1"});
            var Q2;
            Q2=makeQuery(id+"F60.opExtrude","SWEPT_FACE",FACE,{"disambiguationData":[OSD([sQuery(id+"F0.wireOp",EDGE,"E11")])]});
            transform(context, id + "F62", {"entities" : qUnion([Q0, Q1]), "transformType" : TransformType.ROTATION, "transformAxis" : qUnion([Q2]), "angle" : 120 * degree, "oppositeDirection" : true, "makeCopy" : true});
        }
    });
